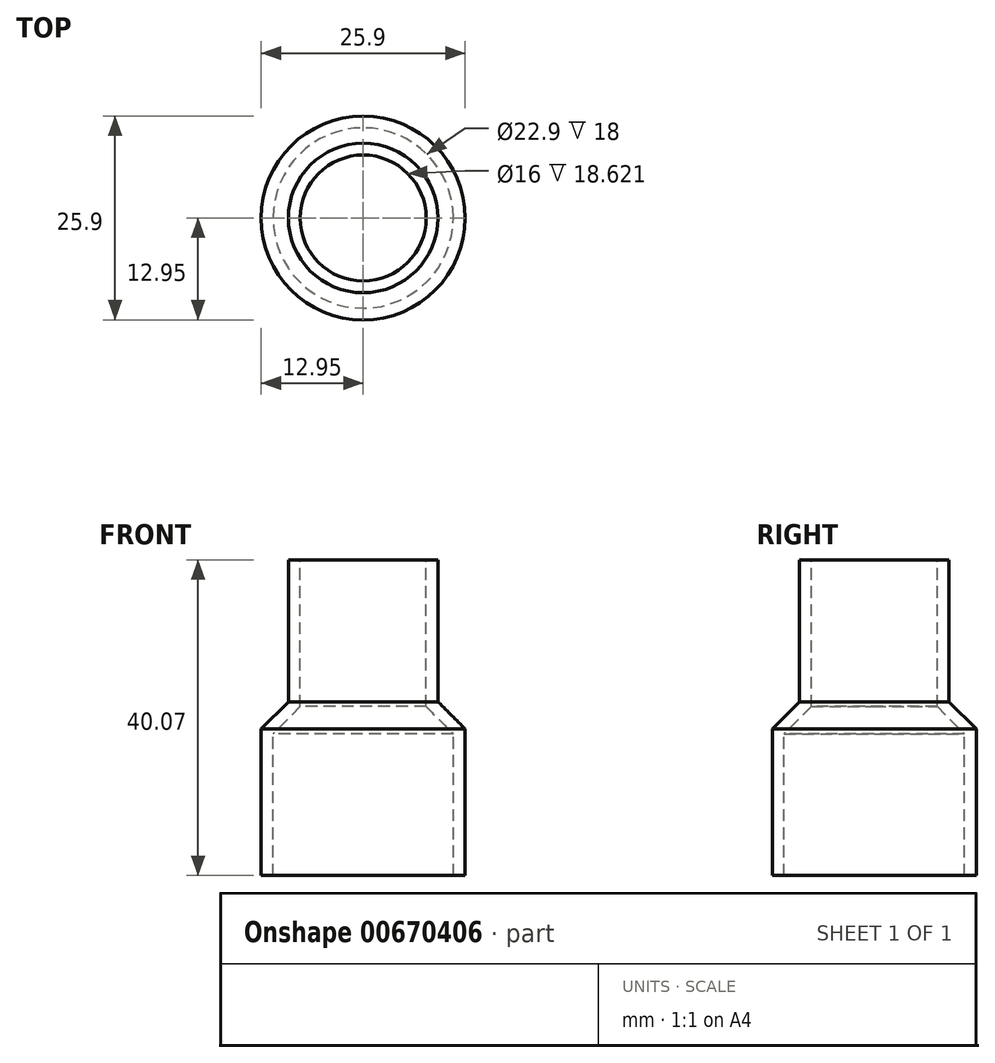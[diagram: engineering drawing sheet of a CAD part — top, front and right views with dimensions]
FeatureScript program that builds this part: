
annotation { "Feature Type Name" : "Feature", "Feature Type Description" : "" }
export const myFeature = defineFeature(function(context is Context, id is Id, definition is map)
    precondition{}
    {
        {
            var Q0;
            Q0=qCreatedBy(makeId("Front.planeOp"),FACE);
            var sketch = newSketch(context, id + "F0", { "sketchPlane" : qUnion([Q0])});
            skLineSegment(sketch, "E0", {"start": v(11.45, 0) * mm, "end": v(12.95, 0) * mm});
            skLineSegment(sketch, "E1", {"start": v(12.95, 0) * mm, "end": v(12.95, 18.62) * mm});
            skLineSegment(sketch, "E2", {"start": v(12.95, 18.62) * mm, "end": v(9.5, 22.07) * mm});
            skLineSegment(sketch, "E3", {"start": v(9.5, 22.07) * mm, "end": v(9.5, 40.07) * mm});
            skLineSegment(sketch, "E4", {"start": v(9.5, 40.07) * mm, "end": v(8, 40.07) * mm});
            skLineSegment(sketch, "E5", {"start": v(8, 40.07) * mm, "end": v(8, 21.45) * mm});
            skLineSegment(sketch, "E6", {"start": v(8, 21.45) * mm, "end": v(11.45, 18) * mm});
            skLineSegment(sketch, "E7", {"start": v(11.45, 18) * mm, "end": v(11.45, 0) * mm});
            skLineSegment(sketch, "E8", {"start": v(0, 49.07) * mm, "end": v(0, -5.19) * mm, "construction": true});
            skSolve(sketch);
        }
        {
            var Q0;
            Q0=makeQuery(id+"F0.imprint","IMPRINT",FACE,{"disambiguationData":[TD([[makeQuery(id+"F0.imprint","IMPRINT",EDGE,{"derivedFrom":sQuery(id+"F0.wireOp",EDGE,"E0")}),1.0]])]});
            var Q1;
            Q1=sQuery(id+"F0.wireOp",EDGE,"E8");
            revolve(context, id + "F1", {"entities" : qUnion([Q0]), "axis" : qUnion([Q1]), "revolveType" : RevolveType.FULL});
        }
    });
